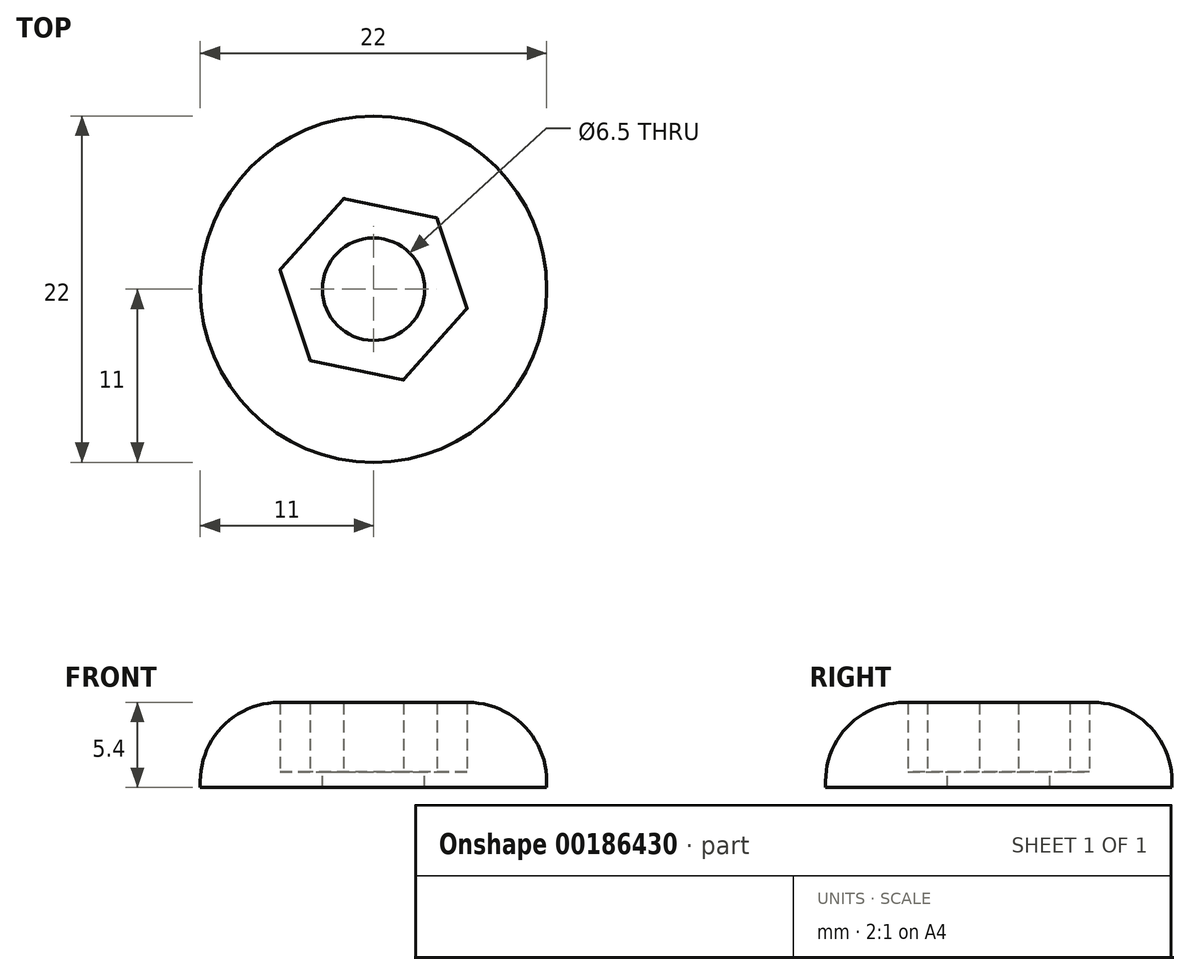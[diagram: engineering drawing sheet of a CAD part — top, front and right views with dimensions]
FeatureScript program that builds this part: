
annotation { "Feature Type Name" : "Feature", "Feature Type Description" : "" }
export const myFeature = defineFeature(function(context is Context, id is Id, definition is map)
    precondition{}
    {
        {
            var Q0;
            Q0=qCreatedBy(makeId("Top.planeOp"),FACE);
            var sketch = newSketch(context, id + "F0", { "sketchPlane" : qUnion([Q0])});
            skCircle(sketch, "E0", {"center": v(0, 0) * mm, "radius": 11 * mm});
            skCircle(sketch, "E1.cCircle", {"center": v(0, 0) * mm, "radius": 5.25 * mm, "construction": true});
            skLineSegment(sketch, "E1.0", {"start": v(5.93, -1.24) * mm, "end": v(1.9, -5.76) * mm});
            skLineSegment(sketch, "E1.1", {"start": v(1.9, -5.76) * mm, "end": v(-4.04, -4.52) * mm});
            skLineSegment(sketch, "E1.2", {"start": v(-4.04, -4.52) * mm, "end": v(-5.93, 1.24) * mm});
            skLineSegment(sketch, "E1.3", {"start": v(-5.93, 1.24) * mm, "end": v(-1.9, 5.76) * mm});
            skLineSegment(sketch, "E1.4", {"start": v(-1.9, 5.76) * mm, "end": v(4.04, 4.52) * mm});
            skLineSegment(sketch, "E1.5", {"start": v(4.04, 4.52) * mm, "end": v(5.93, -1.24) * mm});
            skPoint(sketch, "E1.0.midPoint", {"position": v(3.92, -3.5) * mm});
            skSolve(sketch);
        }
        {
            var Q0;
            Q0=makeQuery(id+"F0.imprint","IMPRINT",FACE,{"disambiguationData":[TD([[makeQuery(id+"F0.imprint","IMPRINT",EDGE,{"derivedFrom":sQuery(id+"F0.wireOp",EDGE,"E0")}),1.0]])]});
            extrude(context, id + "F1", {"entities" : qUnion([Q0]), "depth" : 4.4 * mm});
        }
        {
            var Q0;
            Q0=makeQuery(id+"F1.opExtrude","CAP_FACE",FACE,{"disambiguationData":[OSD([sQuery(id+"F0.wireOp",EDGE,"E0"),sQuery(id+"F0.wireOp",EDGE,"E1.0"),sQuery(id+"F0.wireOp",EDGE,"E1.1"),sQuery(id+"F0.wireOp",EDGE,"E1.2"),sQuery(id+"F0.wireOp",EDGE,"E1.3"),sQuery(id+"F0.wireOp",EDGE,"E1.4"),sQuery(id+"F0.wireOp",EDGE,"E1.5")])],"isStart":true});
            var sketch = newSketch(context, id + "F2", { "sketchPlane" : qUnion([Q0])});
            skCircle(sketch, "E2", {"center": v(0, 0) * mm, "radius": 11 * mm});
            skCircle(sketch, "E3", {"center": v(0, 0) * mm, "radius": 3.25 * mm});
            skSolve(sketch);
        }
        {
            var Q0;
            Q0 = qSketchRegion(id + "F2", true);
            extrude(context, id + "F3", {"entities" : qUnion([Q0]), "operationType" : NewBodyOperationType.ADD, "depth" : 1 * mm});
        }
        {
            var Q0;
            Q0=makeQuery(id+"F1.opExtrude","CAP_EDGE",EDGE,{"disambiguationData":[OSD([sQuery(id+"F0.wireOp",EDGE,"E0")])],"isStart":false});
            fillet(context, id + "F4", {"entities" : qUnion([Q0]), "radius" : 5 * mm, "tangentPropagation" : true, "allowEdgeOverflow" : false});
        }
    });
